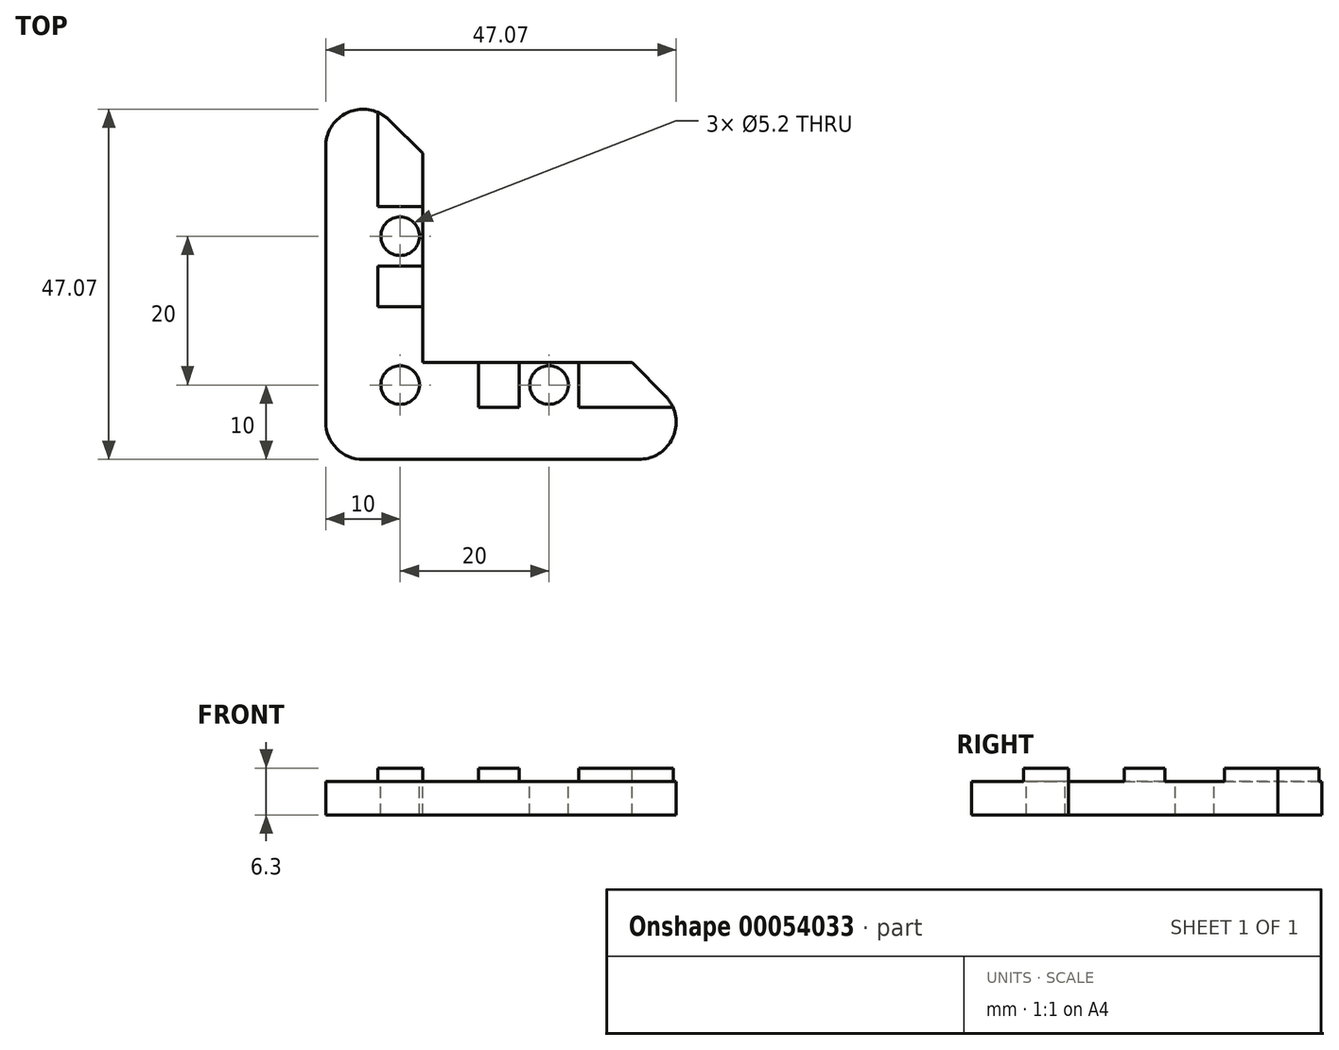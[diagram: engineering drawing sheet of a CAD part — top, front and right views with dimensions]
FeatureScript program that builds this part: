
annotation { "Feature Type Name" : "Feature", "Feature Type Description" : "" }
export const myFeature = defineFeature(function(context is Context, id is Id, definition is map)
    precondition{}
    {
        {
            var Q0;
            Q0=qCreatedBy(makeId("Top.planeOp"),FACE);
            var sketch = newSketch(context, id + "F0", { "sketchPlane" : qUnion([Q0])});
            skLineSegment(sketch, "E0", {"start": v(-76.06, 54.14) * mm, "end": v(-76.06, 0) * mm});
            skLineSegment(sketch, "E1", {"start": v(-76.06, 0) * mm, "end": v(-21.92, 0) * mm});
            skLineSegment(sketch, "E2", {"start": v(-21.92, 0) * mm, "end": v(-76.06, 54.14) * mm});
            skPoint(sketch, "E3", {"position": v(-66.06, 10) * mm});
            skPoint(sketch, "E4", {"position": v(-46.06, 10) * mm});
            skPoint(sketch, "E5", {"position": v(-66.06, 30) * mm});
            skLineSegment(sketch, "E6", {"start": v(-69.06, 0) * mm, "end": v(-69.06, 47.14) * mm});
            skLineSegment(sketch, "E7", {"start": v(-63.06, 0) * mm, "end": v(-63.06, 41.14) * mm});
            skLineSegment(sketch, "E8", {"start": v(-76.06, 13) * mm, "end": v(-34.92, 13) * mm});
            skLineSegment(sketch, "E9", {"start": v(-76.06, 7) * mm, "end": v(-28.92, 7) * mm});
            skLineSegment(sketch, "E10", {"start": v(-55.56, 13) * mm, "end": v(-55.56, 7) * mm});
            skLineSegment(sketch, "E11", {"start": v(-42.06, 13) * mm, "end": v(-42.06, 7) * mm});
            skLineSegment(sketch, "E12", {"start": v(-50.06, 13) * mm, "end": v(-50.06, 7) * mm});
            skLineSegment(sketch, "E13", {"start": v(-69.06, 34) * mm, "end": v(-63.06, 34) * mm});
            skLineSegment(sketch, "E14", {"start": v(-63.06, 34) * mm, "end": v(-63.06, 26) * mm});
            skLineSegment(sketch, "E15", {"start": v(-63.06, 26) * mm, "end": v(-69.06, 26) * mm});
            skLineSegment(sketch, "E16", {"start": v(-69.06, 20.5) * mm, "end": v(-63.06, 20.5) * mm});
            skSolve(sketch);
        }
        {
            var Q0;
            {var subQ5=sQuery(id+"F0.wireOp",EDGE,"E2");var subQ6=sQuery(id+"F0.wireOp",EDGE,"E0");var subQ7=makeQuery(id+"F0.imprint","INTERSECT",VERTEX,{"derivedFrom":[subQ6,subQ5]});Q0=makeQuery(id+"F0.imprint","IMPRINT",FACE,{"disambiguationData":[TD([[makeQuery(id+"F0.imprint","IMPRINT",EDGE,{"disambiguationData":[TD([[subQ7,-1.0]])],"derivedFrom":subQ6}),1.0]])]});}
            var Q1;
            {var subQ5=sQuery(id+"F0.wireOp",EDGE,"E13");Q1=makeQuery(id+"F0.imprint","IMPRINT",FACE,{"disambiguationData":[TD([[makeQuery(id+"F0.imprint","IMPRINT",EDGE,{"derivedFrom":subQ5}),1.0]])]});}
            var Q2;
            {var subQ0=sQuery(id+"F0.wireOp",EDGE,"E13");Q2=makeQuery(id+"F0.imprint","IMPRINT",FACE,{"disambiguationData":[TD([[makeQuery(id+"F0.imprint","IMPRINT",EDGE,{"derivedFrom":subQ0}),-1.0]])]});}
            var Q3;
            {var subQ0=sQuery(id+"F0.wireOp",EDGE,"E15");Q3=makeQuery(id+"F0.imprint","IMPRINT",FACE,{"disambiguationData":[TD([[makeQuery(id+"F0.imprint","IMPRINT",EDGE,{"derivedFrom":subQ0}),1.0]])]});}
            var Q4;
            {var subQ0=sQuery(id+"F0.wireOp",EDGE,"E16");Q4=makeQuery(id+"F0.imprint","IMPRINT",FACE,{"disambiguationData":[TD([[makeQuery(id+"F0.imprint","IMPRINT",EDGE,{"derivedFrom":subQ0}),-1.0]])]});}
            var Q5;
            {var subQ3=sQuery(id+"F0.wireOp",EDGE,"E14");Q5=makeQuery(id+"F0.imprint","IMPRINT",FACE,{"disambiguationData":[TD([[makeQuery(id+"F0.imprint","IMPRINT",EDGE,{"derivedFrom":subQ3}),1.0]])]});}
            var Q6;
            {var subQ0=sQuery(id+"F0.wireOp",EDGE,"E8");var subQ1=sQuery(id+"F0.wireOp",EDGE,"E0");var subQ2=makeQuery(id+"F0.imprint","INTERSECT",VERTEX,{"derivedFrom":[subQ1,subQ0]});Q6=makeQuery(id+"F0.imprint","IMPRINT",FACE,{"disambiguationData":[TD([[makeQuery(id+"F0.imprint","IMPRINT",EDGE,{"disambiguationData":[TD([[subQ2,-1.0]])],"derivedFrom":subQ1}),1.0]])]});}
            var Q7;
            {var subQ0=sQuery(id+"F0.wireOp",EDGE,"E9");var subQ1=sQuery(id+"F0.wireOp",EDGE,"E6");var subQ2=makeQuery(id+"F0.imprint","INTERSECT",VERTEX,{"derivedFrom":[subQ1,subQ0]});Q7=makeQuery(id+"F0.imprint","IMPRINT",FACE,{"disambiguationData":[TD([[makeQuery(id+"F0.imprint","IMPRINT",EDGE,{"disambiguationData":[TD([[subQ2,-1.0]])],"derivedFrom":subQ1}),-1.0]])]});}
            var Q8;
            {var subQ5=sQuery(id+"F0.wireOp",EDGE,"E10");Q8=makeQuery(id+"F0.imprint","IMPRINT",FACE,{"disambiguationData":[TD([[makeQuery(id+"F0.imprint","IMPRINT",EDGE,{"derivedFrom":subQ5}),-1.0]])]});}
            var Q9;
            {var subQ0=sQuery(id+"F0.wireOp",EDGE,"E10");Q9=makeQuery(id+"F0.imprint","IMPRINT",FACE,{"disambiguationData":[TD([[makeQuery(id+"F0.imprint","IMPRINT",EDGE,{"derivedFrom":subQ0}),1.0]])]});}
            var Q10;
            {var subQ0=sQuery(id+"F0.wireOp",EDGE,"E11");Q10=makeQuery(id+"F0.imprint","IMPRINT",FACE,{"disambiguationData":[TD([[makeQuery(id+"F0.imprint","IMPRINT",EDGE,{"derivedFrom":subQ0}),-1.0]])]});}
            var Q11;
            {var subQ5=sQuery(id+"F0.wireOp",EDGE,"E11");Q11=makeQuery(id+"F0.imprint","IMPRINT",FACE,{"disambiguationData":[TD([[makeQuery(id+"F0.imprint","IMPRINT",EDGE,{"derivedFrom":subQ5}),1.0]])]});}
            var Q12;
            {var subQ4=sQuery(id+"F0.wireOp",EDGE,"E1");var subQ6=sQuery(id+"F0.wireOp",EDGE,"E2");var subQ7=makeQuery(id+"F0.imprint","INTERSECT",VERTEX,{"derivedFrom":[subQ4,subQ6]});Q12=makeQuery(id+"F0.imprint","IMPRINT",FACE,{"disambiguationData":[TD([[makeQuery(id+"F0.imprint","IMPRINT",EDGE,{"disambiguationData":[TD([[subQ7,1.0]])],"derivedFrom":subQ4}),1.0]])]});}
            var Q13;
            {var subQ0=sQuery(id+"F0.wireOp",EDGE,"E6");var subQ1=sQuery(id+"F0.wireOp",EDGE,"E1");var subQ2=makeQuery(id+"F0.imprint","INTERSECT",VERTEX,{"derivedFrom":[subQ1,subQ0]});Q13=makeQuery(id+"F0.imprint","IMPRINT",FACE,{"disambiguationData":[TD([[makeQuery(id+"F0.imprint","IMPRINT",EDGE,{"disambiguationData":[TD([[subQ2,-1.0]])],"derivedFrom":subQ1}),1.0]])]});}
            var Q14;
            {var subQ0=sQuery(id+"F0.wireOp",EDGE,"E1");var subQ1=sQuery(id+"F0.wireOp",EDGE,"E0");var subQ2=makeQuery(id+"F0.imprint","INTERSECT",VERTEX,{"derivedFrom":[subQ1,subQ0]});Q14=makeQuery(id+"F0.imprint","IMPRINT",FACE,{"disambiguationData":[TD([[makeQuery(id+"F0.imprint","IMPRINT",EDGE,{"disambiguationData":[TD([[subQ2,1.0]])],"derivedFrom":subQ1}),1.0]])]});}
            extrude(context, id + "F1", {"entities" : qUnion([Q0, Q1, Q2, Q3, Q4, Q5, Q6, Q7, Q8, Q9, Q10, Q11, Q12, Q13, Q14]), "oppositeDirection" : true, "depth" : 4.5 * mm});
        }
        {
            var Q0;
            {var subQ5=sQuery(id+"F0.wireOp",EDGE,"E13");Q0=makeQuery(id+"F0.imprint","IMPRINT",FACE,{"disambiguationData":[TD([[makeQuery(id+"F0.imprint","IMPRINT",EDGE,{"derivedFrom":subQ5}),1.0]])]});}
            var Q1;
            {var subQ0=sQuery(id+"F0.wireOp",EDGE,"E15");Q1=makeQuery(id+"F0.imprint","IMPRINT",FACE,{"disambiguationData":[TD([[makeQuery(id+"F0.imprint","IMPRINT",EDGE,{"derivedFrom":subQ0}),1.0]])]});}
            var Q2;
            {var subQ0=sQuery(id+"F0.wireOp",EDGE,"E10");Q2=makeQuery(id+"F0.imprint","IMPRINT",FACE,{"disambiguationData":[TD([[makeQuery(id+"F0.imprint","IMPRINT",EDGE,{"derivedFrom":subQ0}),1.0]])]});}
            var Q3;
            {var subQ5=sQuery(id+"F0.wireOp",EDGE,"E11");Q3=makeQuery(id+"F0.imprint","IMPRINT",FACE,{"disambiguationData":[TD([[makeQuery(id+"F0.imprint","IMPRINT",EDGE,{"derivedFrom":subQ5}),1.0]])]});}
            extrude(context, id + "F2", {"entities" : qUnion([Q0, Q1, Q2, Q3]), "operationType" : NewBodyOperationType.ADD, "depth" : 1.8 * mm});
        }
        {
            var Q0;
            Q0=sQuery(id+"F0.wireOp",VERTEX,"E5");
            var Q1;
            Q1=sQuery(id+"F0.wireOp",VERTEX,"E3");
            var Q2;
            Q2=sQuery(id+"F0.wireOp",VERTEX,"E4");
            var Q3;
            Q3=makeQuery(id+"F1.opExtrude","SWEPT_BODY",BODY,{"disambiguationData":[OSD([sQuery(id+"F0.wireOp",EDGE,"E0"),sQuery(id+"F0.wireOp",EDGE,"E1"),sQuery(id+"F0.wireOp",EDGE,"E2")])]});
            hole(context, id + "F3", {"style" : HoleStyle.SIMPLE, "holeDiameter" : 5.2 * mm, "endStyle" : HoleEndStyle.THROUGH, "locations" : qUnion([Q0, Q1, Q2]), "scope" : qUnion([Q3])});
        }
        {
            var Q0;
            Q0=makeQuery(id+"F1.opExtrude","SWEPT_EDGE",EDGE,{"disambiguationData":[OSD([sQuery(id+"F0.wireOp",EDGE,"E1"),sQuery(id+"F0.wireOp",EDGE,"E2")])]});
            var Q1;
            Q1=makeQuery(id+"F1.opExtrude","SWEPT_EDGE",EDGE,{"disambiguationData":[OSD([sQuery(id+"F0.wireOp",EDGE,"E0"),sQuery(id+"F0.wireOp",EDGE,"E1")])]});
            var Q2;
            Q2=makeQuery(id+"F1.opExtrude","SWEPT_EDGE",EDGE,{"disambiguationData":[OSD([sQuery(id+"F0.wireOp",EDGE,"E0"),sQuery(id+"F0.wireOp",EDGE,"E2")])]});
            fillet(context, id + "F4", {"entities" : qUnion([Q0, Q1, Q2]), "radius" : 5 * mm, "tangentPropagation" : true, "allowEdgeOverflow" : false});
        }
    });
